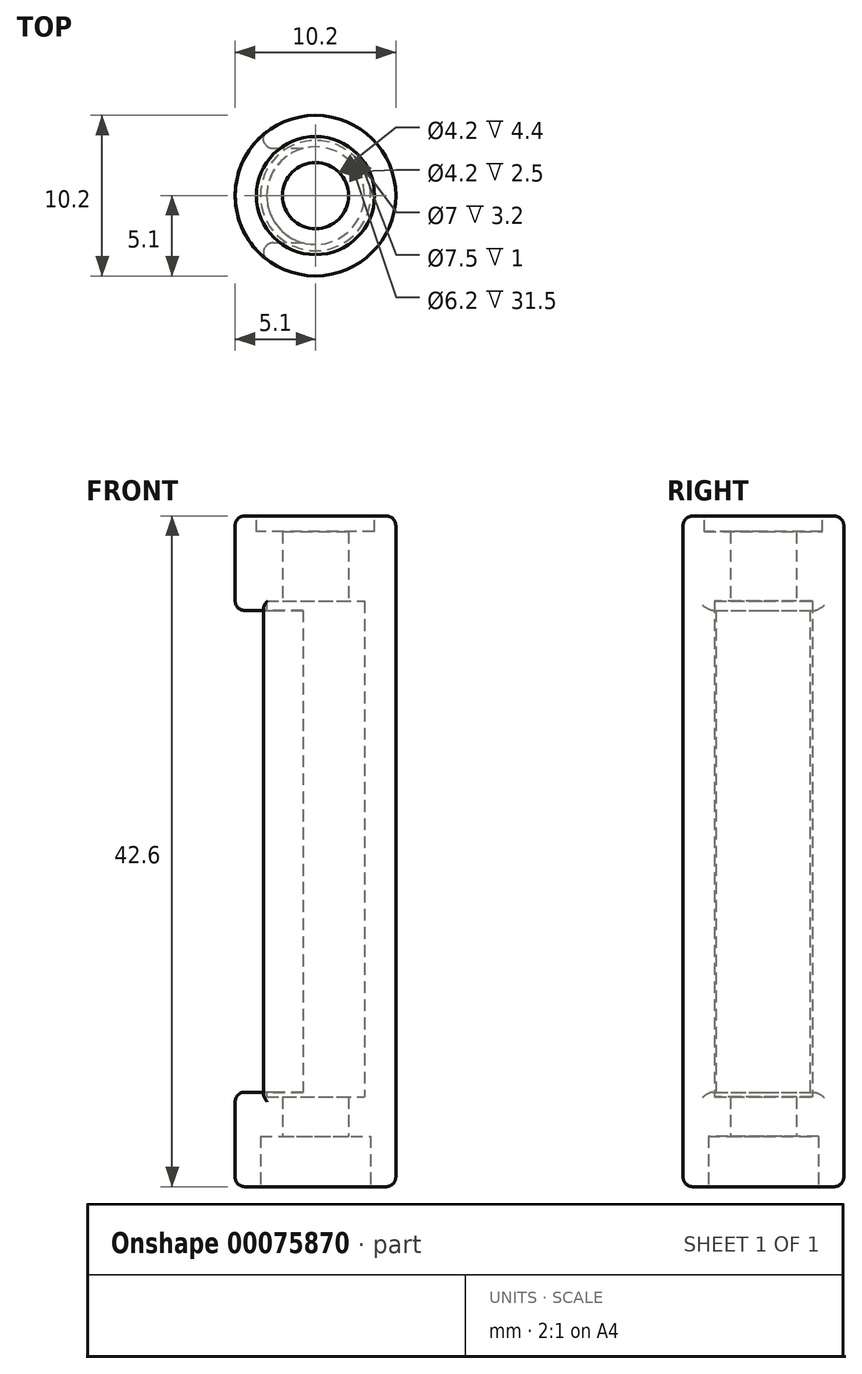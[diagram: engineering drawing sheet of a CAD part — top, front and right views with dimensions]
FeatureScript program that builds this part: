
annotation { "Feature Type Name" : "Feature", "Feature Type Description" : "" }
export const myFeature = defineFeature(function(context is Context, id is Id, definition is map)
    precondition{}
    {
        {
            var Q0;
            Q0=qCreatedBy(makeId("Top.planeOp"),FACE);
            var sketch = newSketch(context, id + "F0", { "sketchPlane" : qUnion([Q0])});
            skCircle(sketch, "E0", {"center": v(0, 0) * mm, "radius": 5.1 * mm});
            skCircle(sketch, "E1", {"center": v(0, 0) * mm, "radius": 2.1 * mm});
            skSolve(sketch);
        }
        {
            var Q0;
            Q0=qSketchRegion(id+"F0",true);
            extrude(context, id + "F1", {"entities" : qUnion([Q0]), "depth" : 42.6 * mm});
        }
        {
            var Q0;
            Q0=makeQuery(id+"F1.opExtrude","CAP_FACE",FACE,{"disambiguationData":[OSD([sQuery(id+"F0.wireOp",EDGE,"E0"),sQuery(id+"F0.wireOp",EDGE,"E1")])],"isStart":true});
            var sketch = newSketch(context, id + "F2", { "sketchPlane" : qUnion([Q0])});
            skCircle(sketch, "E2", {"center": v(0, 0) * mm, "radius": 3.5 * mm});
            skSolve(sketch);
        }
        {
            var Q0;
            Q0=qSketchRegion(id+"F2",true);
            extrude(context, id + "F3", {"entities" : qUnion([Q0]), "operationType" : NewBodyOperationType.REMOVE, "oppositeDirection" : true, "depth" : 3.2 * mm});
        }
        {
            var Q0;
            Q0=makeQuery(id+"F1.opExtrude","CAP_FACE",FACE,{"disambiguationData":[OSD([sQuery(id+"F0.wireOp",EDGE,"E0"),sQuery(id+"F0.wireOp",EDGE,"E1")])],"isStart":false});
            var sketch = newSketch(context, id + "F4", { "sketchPlane" : qUnion([Q0])});
            skCircle(sketch, "E3", {"center": v(0, 0) * mm, "radius": 3.75 * mm});
            skSolve(sketch);
        }
        {
            var Q0;
            Q0=qSketchRegion(id+"F4",true);
            extrude(context, id + "F5", {"entities" : qUnion([Q0]), "operationType" : NewBodyOperationType.REMOVE, "oppositeDirection" : true, "depth" : 1 * mm});
        }
        {
            var Q0;
            Q0=qCreatedBy(makeId("Right.planeOp"),FACE);
            var sketch = newSketch(context, id + "F6", { "sketchPlane" : qUnion([Q0])});
            skLineSegment(sketch, "E4.bottom", {"start": v(-3, 36.6) * mm, "end": v(3, 36.6) * mm});
            skLineSegment(sketch, "E4.top", {"start": v(-3, 6) * mm, "end": v(3, 6) * mm});
            skLineSegment(sketch, "E4.left", {"start": v(-3, 36.6) * mm, "end": v(-3, 6) * mm});
            skLineSegment(sketch, "E4.right", {"start": v(3, 36.6) * mm, "end": v(3, 6) * mm});
            skPoint(sketch, "E4.middle", {"position": v(0, 21.3) * mm});
            skSolve(sketch);
        }
        {
            var Q0;
            Q0=qSketchRegion(id+"F6",true);
            extrude(context, id + "F7", {"entities" : qUnion([Q0]), "operationType" : NewBodyOperationType.REMOVE, "oppositeDirection" : true, "depth" : 25 * mm});
        }
        {
            var Q0;
            Q0=makeQuery(id+"F3.boolean.opBoolean","COPY",FACE,{"derivedFrom":makeQuery(id+"F3.opExtrude","CAP_FACE",FACE,{"disambiguationData":[OSD([sQuery(id+"F2.wireOp",EDGE,"E2")])],"isStart":false})});
            var sketch = newSketch(context, id + "F8", { "sketchPlane" : qUnion([Q0])});
            skCircle(sketch, "E5", {"center": v(0, 0) * mm, "radius": 3.1 * mm});
            skSolve(sketch);
        }
        {
            var Q0;
            Q0=qSketchRegion(id+"F8",true);
            extrude(context, id + "F9", {"entities" : qUnion([Q0]), "operationType" : NewBodyOperationType.REMOVE, "oppositeDirection" : true, "depth" : 34 * mm, "hasSecondDirection" : true, "secondDirectionOppositeDirection" : true, "secondDirectionDepth" : 2.5 * mm});
        }
        {
            var Q0;
            Q0=makeQuery(id+"F1.opExtrude","CAP_EDGE",EDGE,{"disambiguationData":[OSD([sQuery(id+"F0.wireOp",EDGE,"E0")])],"isStart":false});
            var Q1;
            Q1=makeQuery(id+"F1.opExtrude","CAP_EDGE",EDGE,{"disambiguationData":[OSD([sQuery(id+"F0.wireOp",EDGE,"E0")])],"isStart":true});
            var Q2;
            Q2=makeQuery(id+"F7.boolean.opBoolean","INTERSECT",EDGE,{"derivedFrom":[makeQuery(id+"F1.opExtrude","SWEPT_FACE",FACE,{"disambiguationData":[OSD([sQuery(id+"F0.wireOp",EDGE,"E0")])]}),makeQuery(id+"F7.opExtrude","SWEPT_FACE",FACE,{"disambiguationData":[OSD([sQuery(id+"F6.wireOp",EDGE,"E4.top")])]})]});
            var Q3;
            Q3=makeQuery(id+"F7.boolean.opBoolean","INTERSECT",EDGE,{"derivedFrom":[makeQuery(id+"F1.opExtrude","SWEPT_FACE",FACE,{"disambiguationData":[OSD([sQuery(id+"F0.wireOp",EDGE,"E0")])]}),makeQuery(id+"F7.opExtrude","SWEPT_FACE",FACE,{"disambiguationData":[OSD([sQuery(id+"F6.wireOp",EDGE,"E4.right")])]})]});
            var Q4;
            Q4=makeQuery(id+"F7.boolean.opBoolean","INTERSECT",EDGE,{"derivedFrom":[makeQuery(id+"F1.opExtrude","SWEPT_FACE",FACE,{"disambiguationData":[OSD([sQuery(id+"F0.wireOp",EDGE,"E0")])]}),makeQuery(id+"F7.opExtrude","SWEPT_FACE",FACE,{"disambiguationData":[OSD([sQuery(id+"F6.wireOp",EDGE,"E4.left")])]})]});
            var Q5;
            Q5=makeQuery(id+"F7.boolean.opBoolean","INTERSECT",EDGE,{"derivedFrom":[makeQuery(id+"F1.opExtrude","SWEPT_FACE",FACE,{"disambiguationData":[OSD([sQuery(id+"F0.wireOp",EDGE,"E0")])]}),makeQuery(id+"F7.opExtrude","SWEPT_FACE",FACE,{"disambiguationData":[OSD([sQuery(id+"F6.wireOp",EDGE,"E4.bottom")])]})]});
            fillet(context, id + "F10", {"entities" : qUnion([Q0, Q1, Q2, Q3, Q4, Q5]), "radius" : 0.6 * mm, "tangentPropagation" : true, "allowEdgeOverflow" : false});
        }
    });
